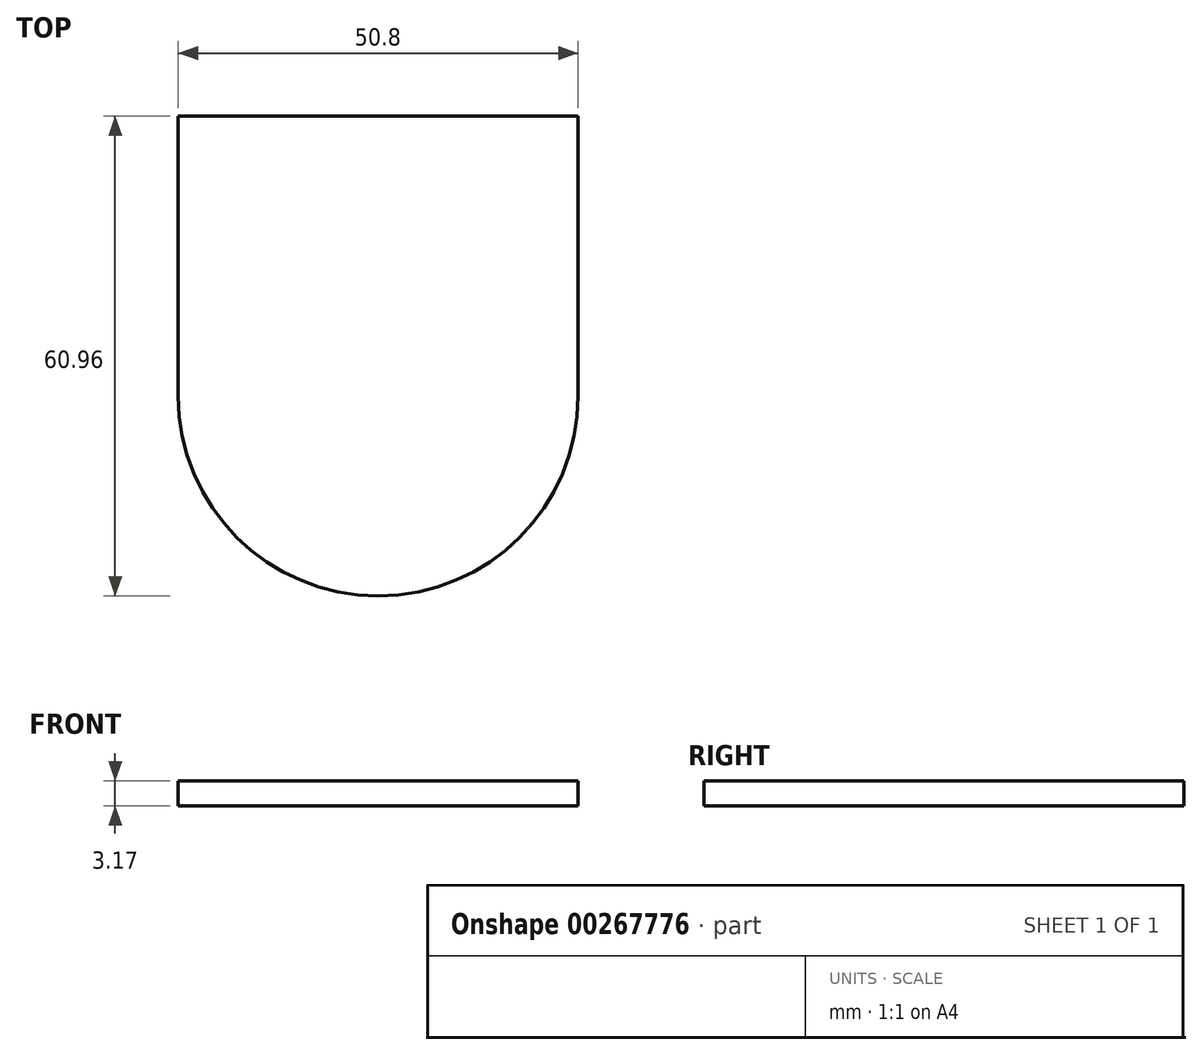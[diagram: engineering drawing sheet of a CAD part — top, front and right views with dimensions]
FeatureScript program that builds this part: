
annotation { "Feature Type Name" : "Feature", "Feature Type Description" : "" }
export const myFeature = defineFeature(function(context is Context, id is Id, definition is map)
    precondition{}
    {
        {
            var Q0;
            Q0=qCreatedBy(makeId("Top.planeOp"),FACE);
            var sketch = newSketch(context, id + "F0", { "sketchPlane" : qUnion([Q0])});
            skLineSegment(sketch, "E0", {"start": v(0, 0) * mm, "end": v(0, 35.56) * mm});
            skLineSegment(sketch, "E1", {"start": v(0, 35.56) * mm, "end": v(-25.4, 35.56) * mm});
            skLineSegment(sketch, "E2", {"start": v(0, 35.56) * mm, "end": v(25.4, 35.56) * mm});
            skLineSegment(sketch, "E3", {"start": v(-25.4, 35.56) * mm, "end": v(-25.4, 0) * mm});
            skLineSegment(sketch, "E4", {"start": v(-25.4, 0) * mm, "end": v(0, 0) * mm});
            skCircle(sketch, "E5", {"center": v(0, 0) * mm, "radius": 25.4 * mm});
            skLineSegment(sketch, "E6", {"start": v(25.4, 35.56) * mm, "end": v(25.4, 0) * mm});
            skSolve(sketch);
        }
        {
            var Q0;
            {var subQ0=sQuery(id+"F0.wireOp",EDGE,"E1");Q0=makeQuery(id+"F0.imprint","IMPRINT",FACE,{"disambiguationData":[TD([[makeQuery(id+"F0.imprint","IMPRINT",EDGE,{"derivedFrom":subQ0}),1.0]])]});}
            var Q1;
            {var subQ0=sQuery(id+"F0.wireOp",EDGE,"E2");Q1=makeQuery(id+"F0.imprint","IMPRINT",FACE,{"disambiguationData":[TD([[makeQuery(id+"F0.imprint","IMPRINT",EDGE,{"derivedFrom":subQ0}),-1.0]])]});}
            var Q2;
            {var subQ0=sQuery(id+"F0.wireOp",EDGE,"E4");Q2=makeQuery(id+"F0.imprint","IMPRINT",FACE,{"disambiguationData":[TD([[makeQuery(id+"F0.imprint","IMPRINT",EDGE,{"derivedFrom":subQ0}),1.0]])]});}
            var Q3;
            {var subQ0=sQuery(id+"F0.wireOp",EDGE,"E4");Q3=makeQuery(id+"F0.imprint","IMPRINT",FACE,{"disambiguationData":[TD([[makeQuery(id+"F0.imprint","IMPRINT",EDGE,{"derivedFrom":subQ0}),-1.0]])]});}
            extrude(context, id + "F1", {"entities" : qUnion([Q0, Q1, Q2, Q3]), "depth" : 3.17 * mm});
        }
    });
